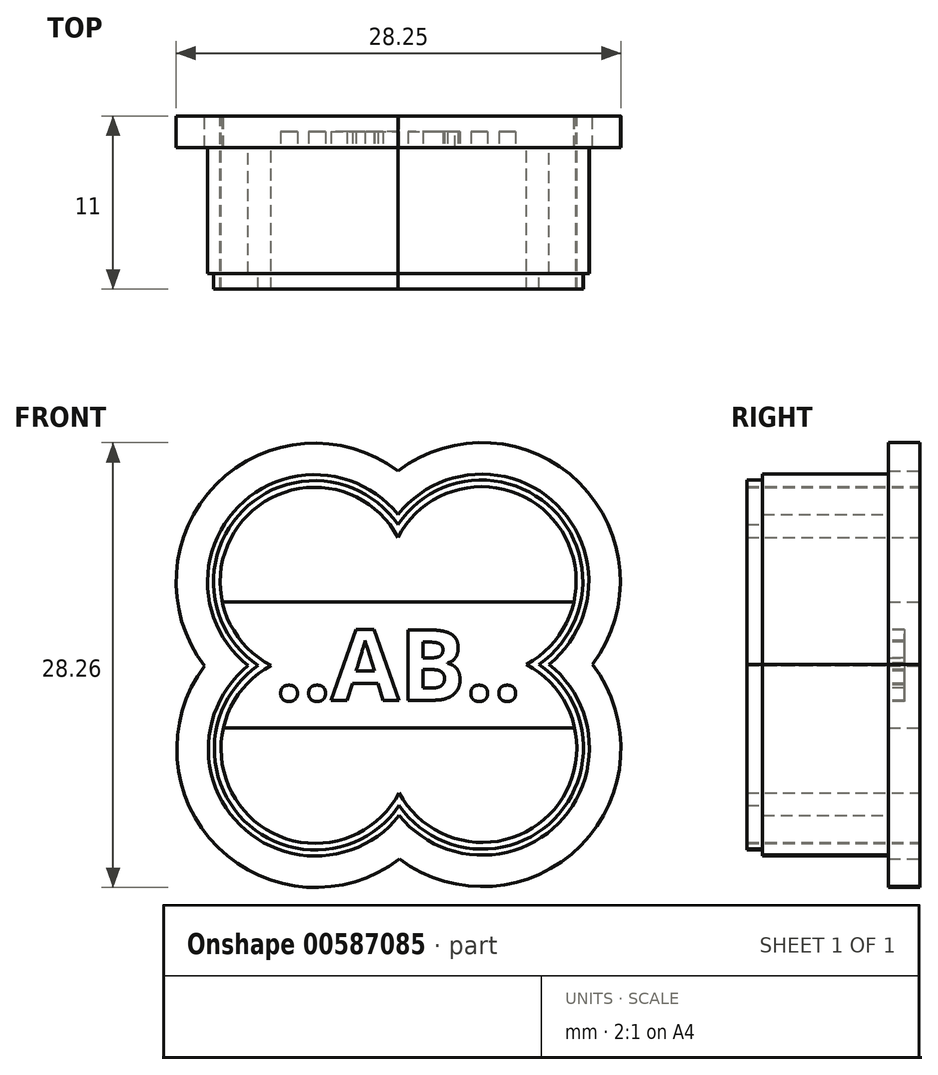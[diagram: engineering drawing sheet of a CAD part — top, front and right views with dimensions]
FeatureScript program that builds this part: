
annotation { "Feature Type Name" : "Feature", "Feature Type Description" : "" }
export const myFeature = defineFeature(function(context is Context, id is Id, definition is map)
    precondition{}
    {
        {
            var Q0;
            Q0=qCreatedBy(makeId("Front.planeOp"),FACE);
            var sketch = newSketch(context, id + "F0", { "sketchPlane" : qUnion([Q0])});
            skArc(sketch, "E0", {"start": v(-0.03, 8.1) * mm, "mid": v(-9.59, 9.5) * mm, "end": v(-8.1, -0.04) * mm});
            skArc(sketch, "E1", {"start": v(-8.1, -0.04) * mm, "mid": v(-9.5, -9.6) * mm, "end": v(0.04, -8.12) * mm});
            skArc(sketch, "E2.trimOffspring", {"start": v(8.12, 0.03) * mm, "mid": v(9.5, 9.58) * mm, "end": v(-0.03, 8.1) * mm});
            skArc(sketch, "E3.trimOffspring", {"start": v(0.04, -8.12) * mm, "mid": v(9.59, -9.5) * mm, "end": v(8.12, 0.03) * mm});
            skArc(sketch, "E4.0", {"start": v(-0.03, 8.92) * mm, "mid": v(-9.89, 9.8) * mm, "end": v(-8.9, -0.04) * mm});
            skArc(sketch, "E4.1", {"start": v(8.93, 0.03) * mm, "mid": v(9.8, 9.88) * mm, "end": v(-0.03, 8.92) * mm});
            skArc(sketch, "E4.2", {"start": v(0.05, -8.93) * mm, "mid": v(9.89, -9.8) * mm, "end": v(8.93, 0.03) * mm});
            skArc(sketch, "E4.3", {"start": v(-8.9, -0.04) * mm, "mid": v(-9.8, -9.9) * mm, "end": v(0.05, -8.93) * mm});
            skSolve(sketch);
        }
        {
            var Q0;
            Q0 = qSketchRegion(id + "F0", true);
            extrude(context, id + "F1", {"entities" : qUnion([Q0]), "depth" : 11 * mm, "offsetDistance" : 25 * mm});
        }
        {
            var Q0;
            Q0=qCreatedBy(makeId("Front.planeOp"),FACE);
            var sketch = newSketch(context, id + "F2", { "sketchPlane" : qUnion([Q0])});
            skArc(sketch, "E5.0", {"start": v(-9.55, -0.05) * mm, "mid": v(-10.06, -10.16) * mm, "end": v(0.05, -9.57) * mm});
            skArc(sketch, "E5.1", {"start": v(-0.03, 9.56) * mm, "mid": v(-10.15, 10.07) * mm, "end": v(-9.55, -0.05) * mm});
            skArc(sketch, "E5.2", {"start": v(9.57, 0.04) * mm, "mid": v(10.07, 10.15) * mm, "end": v(-0.03, 9.56) * mm});
            skArc(sketch, "E5.3", {"start": v(0.05, -9.57) * mm, "mid": v(10.16, -10.07) * mm, "end": v(9.57, 0.04) * mm});
            skSolve(sketch);
        }
        {
            var Q0;
            Q0 = qSketchRegion(id + "F2", true);
            extrude(context, id + "F3", {"entities" : qUnion([Q0]), "operationType" : NewBodyOperationType.ADD, "depth" : 10 * mm, "offsetDistance" : 25 * mm});
        }
        {
            var Q0;
            Q0=makeQuery(id+"F3.boolean.opBoolean","SPLIT",FACE,{"disambiguationData":[TD([makeQuery(id+"F1.opExtrude","SWEPT_FACE",FACE,{"disambiguationData":[OSD([sQuery(id+"F0.wireOp",EDGE,"E0")])]})])],"derivedFrom":makeQuery(id+"F3.opExtrude","CAP_FACE",FACE,{"disambiguationData":[OSD([sQuery(id+"F2.wireOp",EDGE,"E5.0"),sQuery(id+"F2.wireOp",EDGE,"E5.1"),sQuery(id+"F2.wireOp",EDGE,"E5.2"),sQuery(id+"F2.wireOp",EDGE,"E5.3")])],"isStart":false})});
            var sketch = newSketch(context, id + "F4", { "sketchPlane" : qUnion([Q0])});
            skSolve(sketch);
        }
        {
            var Q0;
            {var subQ0=makeQuery(id+"F3.opExtrude","CAP_FACE",FACE,{"disambiguationData":[OSD([sQuery(id+"F2.wireOp",EDGE,"E5.0"),sQuery(id+"F2.wireOp",EDGE,"E5.1"),sQuery(id+"F2.wireOp",EDGE,"E5.2"),sQuery(id+"F2.wireOp",EDGE,"E5.3")])],"isStart":false});Q0=makeQuery(id+"F4.imprint","IMPRINT",FACE,{"disambiguationData":[TD([[makeQuery(id+"F4.imprint","IMPRINT",EDGE,{"derivedFrom":makeQuery(id+"F3.boolean.opBoolean","INTERSECT",EDGE,{"derivedFrom":[makeQuery(id+"F1.opExtrude","SWEPT_FACE",FACE,{"disambiguationData":[OSD([sQuery(id+"F0.wireOp",EDGE,"E0")])]}),subQ0]})}),1.0]])]});}
            extrude(context, id + "F5", {"entities" : qUnion([Q0]), "operationType" : NewBodyOperationType.REMOVE, "oppositeDirection" : true, "depth" : 10 * mm, "offsetDistance" : 25 * mm});
        }
        {
            var Q0;
            Q0=qCreatedBy(makeId("Front.planeOp"),FACE);
            var sketch = newSketch(context, id + "F6", { "sketchPlane" : qUnion([Q0])});
            skArc(sketch, "E6.0", {"start": v(-12.31, -0.06) * mm, "mid": v(-11.47, -11.59) * mm, "end": v(0.07, -12.33) * mm});
            skArc(sketch, "E6.1", {"start": v(-0.04, 12.32) * mm, "mid": v(-11.57, 11.48) * mm, "end": v(-12.31, -0.06) * mm});
            skArc(sketch, "E6.2", {"start": v(12.33, 0.05) * mm, "mid": v(11.48, 11.57) * mm, "end": v(-0.04, 12.32) * mm});
            skArc(sketch, "E6.3", {"start": v(0.07, -12.33) * mm, "mid": v(11.58, -11.47) * mm, "end": v(12.33, 0.05) * mm});
            skSolve(sketch);
        }
        {
            var Q0;
            Q0 = qSketchRegion(id + "F6", true);
            extrude(context, id + "F7", {"entities" : qUnion([Q0]), "operationType" : NewBodyOperationType.ADD, "depth" : 2 * mm, "offsetDistance" : 25 * mm});
        }
        {
            var Q0;
            {var subQ3=sQuery(id+"F0.wireOp",EDGE,"E0");Q0=makeQuery(id+"F7.boolean.opBoolean","SPLIT",FACE,{"disambiguationData":[TD([makeQuery(id+"F1.opExtrude","SWEPT_FACE",FACE,{"disambiguationData":[OSD([subQ3])]})])],"derivedFrom":makeQuery(id+"F7.opExtrude","CAP_FACE",FACE,{"disambiguationData":[OSD([sQuery(id+"F6.wireOp",EDGE,"E6.0"),sQuery(id+"F6.wireOp",EDGE,"E6.1"),sQuery(id+"F6.wireOp",EDGE,"E6.2"),sQuery(id+"F6.wireOp",EDGE,"E6.3")])],"isStart":false})});}
            var sketch = newSketch(context, id + "F8", { "sketchPlane" : qUnion([Q0])});
            skSolve(sketch);
        }
        {
            var Q0;
            {var subQ0=makeQuery(id+"F7.opExtrude","CAP_FACE",FACE,{"disambiguationData":[OSD([sQuery(id+"F6.wireOp",EDGE,"E6.0"),sQuery(id+"F6.wireOp",EDGE,"E6.1"),sQuery(id+"F6.wireOp",EDGE,"E6.2"),sQuery(id+"F6.wireOp",EDGE,"E6.3")])],"isStart":false});var subQ1=sQuery(id+"F2.wireOp",EDGE,"E5.3");var subQ2=sQuery(id+"F2.wireOp",EDGE,"E5.2");var subQ3=sQuery(id+"F2.wireOp",EDGE,"E5.1");var subQ4=sQuery(id+"F2.wireOp",EDGE,"E5.0");var subQ5=sQuery(id+"F0.wireOp",EDGE,"E0");Q0=makeQuery(id+"F8.imprint","IMPRINT",FACE,{"disambiguationData":[TD([[makeQuery(id+"F8.imprint","IMPRINT",EDGE,{"derivedFrom":makeQuery(id+"F7.boolean.opBoolean","INTERSECT",EDGE,{"derivedFrom":[makeQuery(id+"F5.boolean.opBoolean","MERGE",FACE,{"derivedFrom":[makeQuery(id+"F1.opExtrude","SWEPT_FACE",FACE,{"disambiguationData":[OSD([subQ5])]}),makeQuery(id+"F5.opExtrude","SWEPT_FACE",FACE,{"disambiguationData":[OSD([subQ5,subQ4,subQ3,subQ2,subQ1])]})]}),subQ0]})}),1.0]])]});}
            cPlane(context, id + "F9", {"entities" : qUnion([Q0]), "cplaneType" : CPlaneType.OFFSET, "offset" : 0 * mm, "width" : 150 * mm, "height" : 150 * mm});
        }
        {
            var Q0;
            {var subQ0=makeQuery(id+"F7.opExtrude","CAP_FACE",FACE,{"disambiguationData":[OSD([sQuery(id+"F6.wireOp",EDGE,"E6.0"),sQuery(id+"F6.wireOp",EDGE,"E6.1"),sQuery(id+"F6.wireOp",EDGE,"E6.2"),sQuery(id+"F6.wireOp",EDGE,"E6.3")])],"isStart":false});var subQ1=sQuery(id+"F2.wireOp",EDGE,"E5.3");var subQ2=sQuery(id+"F2.wireOp",EDGE,"E5.2");var subQ3=sQuery(id+"F2.wireOp",EDGE,"E5.1");var subQ4=sQuery(id+"F2.wireOp",EDGE,"E5.0");var subQ5=sQuery(id+"F0.wireOp",EDGE,"E0");Q0=makeQuery(id+"F8.imprint","IMPRINT",FACE,{"disambiguationData":[TD([[makeQuery(id+"F8.imprint","IMPRINT",EDGE,{"derivedFrom":makeQuery(id+"F7.boolean.opBoolean","INTERSECT",EDGE,{"derivedFrom":[makeQuery(id+"F5.boolean.opBoolean","MERGE",FACE,{"derivedFrom":[makeQuery(id+"F1.opExtrude","SWEPT_FACE",FACE,{"disambiguationData":[OSD([subQ5])]}),makeQuery(id+"F5.opExtrude","SWEPT_FACE",FACE,{"disambiguationData":[OSD([subQ5,subQ4,subQ3,subQ2,subQ1])]})]}),subQ0]})}),1.0]])]});}
            extrude(context, id + "F10", {"entities" : qUnion([Q0]), "operationType" : NewBodyOperationType.REMOVE, "oppositeDirection" : true, "depth" : 2 * mm, "offsetDistance" : 25 * mm});
        }
        {
            var Q0;
            Q0=qCreatedBy(id+"F9.planeOp",FACE);
            var sketch = newSketch(context, id + "F11", { "sketchPlane" : qUnion([Q0])});
            skLineSegment(sketch, "E7.bottom", {"start": v(-11.92, 0) * mm, "end": v(11.56, 0) * mm});
            skLineSegment(sketch, "E7.top", {"start": v(-11.92, 4) * mm, "end": v(11.56, 4) * mm});
            skLineSegment(sketch, "E7.left", {"start": v(-11.92, 0) * mm, "end": v(-11.92, 4) * mm});
            skLineSegment(sketch, "E7.right", {"start": v(11.56, 0) * mm, "end": v(11.56, 4) * mm});
            skLineSegment(sketch, "E8.top", {"start": v(-11.92, -4) * mm, "end": v(11.56, -4) * mm});
            skLineSegment(sketch, "E8.left", {"start": v(-11.92, 0) * mm, "end": v(-11.92, -4) * mm});
            skLineSegment(sketch, "E8.right", {"start": v(11.56, 0) * mm, "end": v(11.56, -4) * mm});
            skLineSegment(sketch, "E9.bottom", {"start": v(0, 11.34) * mm, "end": v(-4, 11.34) * mm});
            skLineSegment(sketch, "E10.bottom", {"start": v(0, 11.34) * mm, "end": v(4, 11.34) * mm});
            skSolve(sketch);
        }
        {
            var Q0;
            Q0 = qSketchRegion(id + "F11", true);
            extrude(context, id + "F12", {"entities" : qUnion([Q0]), "operationType" : NewBodyOperationType.ADD, "oppositeDirection" : true, "depth" : 2 * mm, "offsetDistance" : 25 * mm});
        }
        {
            var Q0;
            Q0=makeQuery(id+"F12.opExtrude","CAP_FACE",FACE,{"disambiguationData":[OSD([sQuery(id+"F11.wireOp",EDGE,"E7.top"),sQuery(id+"F11.wireOp",EDGE,"E7.left"),sQuery(id+"F11.wireOp",EDGE,"E7.right"),sQuery(id+"F11.wireOp",EDGE,"E8.top"),sQuery(id+"F11.wireOp",EDGE,"E8.left"),sQuery(id+"F11.wireOp",EDGE,"E8.right"),sQuery(id+"F11.wireOp",EDGE,"E9.bottom"),sQuery(id+"F11.wireOp",EDGE,"E9.top"),sQuery(id+"F11.wireOp",EDGE,"E9.left"),sQuery(id+"F11.wireOp",EDGE,"E9.right"),sQuery(id+"F11.wireOp",EDGE,"E10.bottom"),sQuery(id+"F11.wireOp",EDGE,"E10.top"),sQuery(id+"F11.wireOp",EDGE,"E10.right")])],"isStart":true});
            cPlane(context, id + "F13", {"entities" : qUnion([Q0]), "cplaneType" : CPlaneType.OFFSET, "offset" : 0 * mm, "width" : 150 * mm, "height" : 150 * mm});
        }
        {
            var Q0;
            Q0=qCreatedBy(id+"F13.planeOp",FACE);
            var sketch = newSketch(context, id + "F14", { "sketchPlane" : qUnion([Q0])});
            skText(sketch, "E11", { "text": "..AB..", "fontName": "OpenSans-Bold.ttf"});
            const initialGuessF14  = {"E11": [-0.00784, -0.00224, 1, 0, 0.0045]};
            skSetInitialGuess(sketch, initialGuessF14);
            skSolve(sketch);
        }
        {
            var Q0;
            Q0 = qSketchRegion(id + "F14", true);
            extrude(context, id + "F15", {"entities" : qUnion([Q0]), "operationType" : NewBodyOperationType.REMOVE, "oppositeDirection" : true, "depth" : 1 * mm, "offsetDistance" : 25 * mm});
        }
    });
